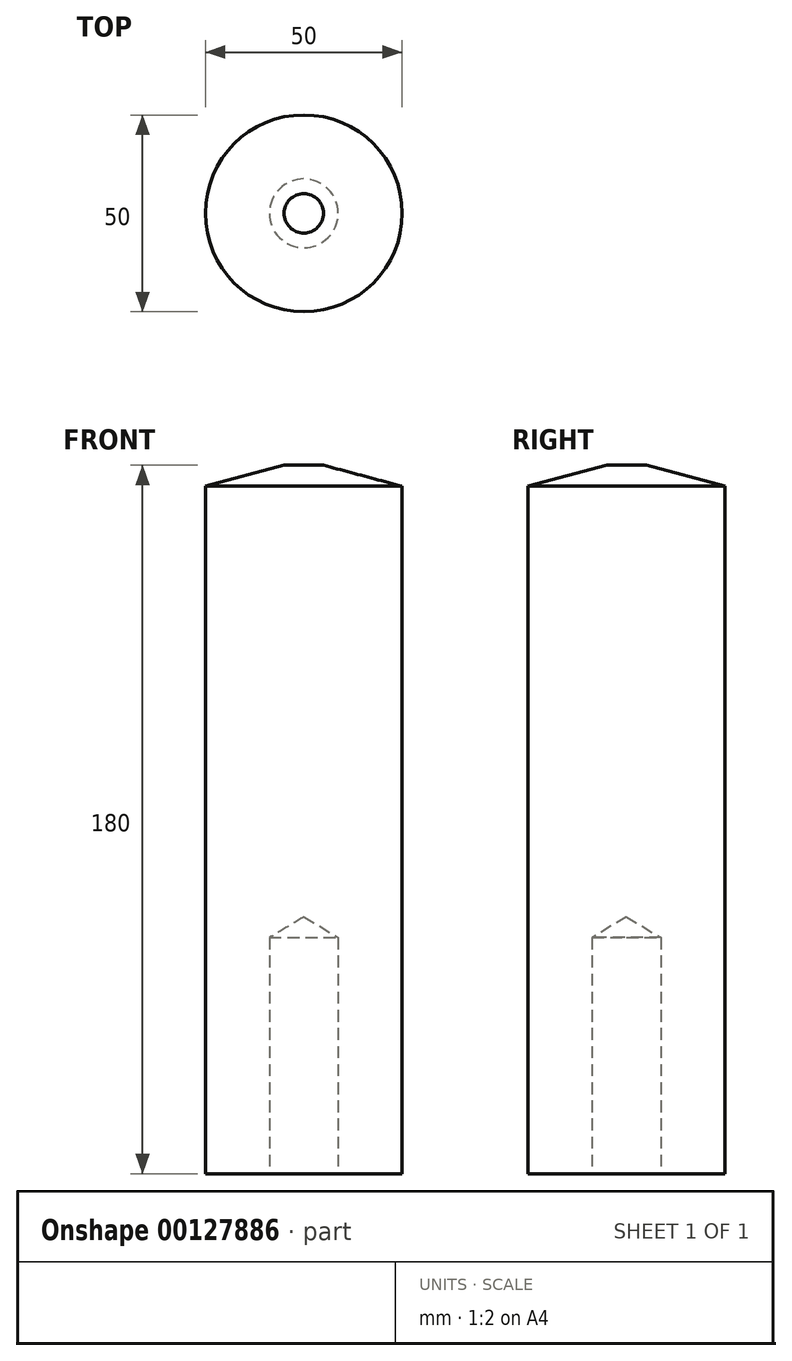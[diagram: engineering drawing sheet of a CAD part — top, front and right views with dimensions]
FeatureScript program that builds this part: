
annotation { "Feature Type Name" : "Feature", "Feature Type Description" : "" }
export const myFeature = defineFeature(function(context is Context, id is Id, definition is map)
    precondition{}
    {
        {
            var Q0;
            Q0=qCreatedBy(makeId("Top.planeOp"),FACE);
            var sketch = newSketch(context, id + "F0", { "sketchPlane" : qUnion([Q0])});
            skCircle(sketch, "E0", {"center": v(0, 0) * mm, "radius": 25 * mm});
            skSolve(sketch);
        }
        {
            var Q0;
            Q0 = qSketchRegion(id + "F0", true);
            extrude(context, id + "F1", {"entities" : qUnion([Q0]), "depth" : 180 * mm});
        }
        {
            var Q0;
            Q0=makeQuery(id+"F1.opExtrude","CAP_EDGE",EDGE,{"disambiguationData":[OSD([sQuery(id+"F0.wireOp",EDGE,"E0")])],"isStart":false});
            chamfer(context, id + "F2", {"entities" : qUnion([Q0]), "chamferType" : ChamferType.OFFSET_ANGLE, "width" : 20 * mm, "oppositeDirection" : false, "angle" : 15 * degree, "tangentPropagation" : true});
        }
        {
            var Q0;
            Q0=makeQuery(id+"F1.opExtrude","CAP_FACE",FACE,{"disambiguationData":[OSD([sQuery(id+"F0.wireOp",EDGE,"E0")])],"isStart":true});
            var sketch = newSketch(context, id + "F3", { "sketchPlane" : qUnion([Q0])});
            skCircle(sketch, "E1", {"center": v(0, 0) * mm, "radius": 8 * mm});
            skSolve(sketch);
        }
        {
            var Q0;
            Q0=sQuery(id+"F3.wireOp",VERTEX,"E1.center");
            var Q1;
            Q1=makeQuery(id+"F1.opExtrude","SWEPT_BODY",BODY,{"disambiguationData":[OSD([sQuery(id+"F0.wireOp",EDGE,"E0")])]});
            hole(context, id + "F4", {"style" : HoleStyle.SIMPLE, "endStyle" : HoleEndStyle.BLIND, "standardTappedOrClearance" : lookupTablePath({ "standard" : "ISO", "fit" : "Normal", "size" : "M16", "type" : "Clearance" }), "standardBlindInLast" : lookupTablePath({ "fit" : "Standard", "standard" : "ISO", "size" : "M16", "type" : "Clearance" }), "holeDiameter" : 17.5 * mm, "holeDepth" : 60 * mm, "startFromSketch" : true, "locations" : qUnion([Q0]), "scope" : qUnion([Q1])});
        }
    });
